# Revit family: Faucet-Kitchen-KOHLER-Elate-K-13963T-1
name_source: partatom
category: Plumbing Fixtures
units: mm (PartAtom-declared; Revit-internal decimal feet)

## family parameters
Cut with Voids When Loaded = No
Host = Face
OmniClass Number = 23.31.11.00
Part Type = Normal
Room Calculation Point = No
Round Connector Dimension = Use Diameter
Shared = No

## types (3) — shared parameters
ADA Compliant = No
Assembly Code = D2010
CW Connection = Yes
Cold Water Inlet = Cold Water Inlet
Date Modified = 08/26/2024
Default Elevation = 36"
Drain Included = No
Flow Rate = 0 GPM
HW Connection = Yes
Handle Clearance = 3 1/4"
Height = 11 15/16"
Hot Water Inlet = Hot Water Inlet
Length = 9"
Manufacturer = Kohler Co.
MasterFormat 2004 Name = 22.41.39
MasterFormat 2014 = 15410
Material = Cast copper body
Pressure = 0.00 psi
Product Documentation Link = http://files.kohler.com.cn
Product Name = ELATE
Product Page URL = http://www.kohler.com.cn
Spout Reach = 9"
URL = http://www.kohler.com.cn
Vent Connection = No
Waste Connection = No
Waste Water Outlet = Waste Water Outlet
WaterSense Certified = No
Width = 2"

## per-type parameters (varying)
| type | Description | Finish | Model | Type |
| ECP-Easy To Clean Plating | Pull-out kitchen faucet (easy to clean surface) | Kohler-Metal-ECP-PVD_Coated_Polished_Chrome | K-13963T-C4-ECP | 1 |
| CP-Polished Chrome | Pull-out kitchen faucet | Kohler-Metal-CP-Polished_Chrome | K-13963T-C4-CP | 2 |
| VS-Stainless Steel Wire Drawing | Pull-out kitchen faucet | Kohler-Metal-VS-Stainless_Steel_Wire_Drawing | K-13963T-C4-VS | 3 |

## geometry (parser evidence)
native form markers: Sweep x5
no freeform markers — native parametric forms only
